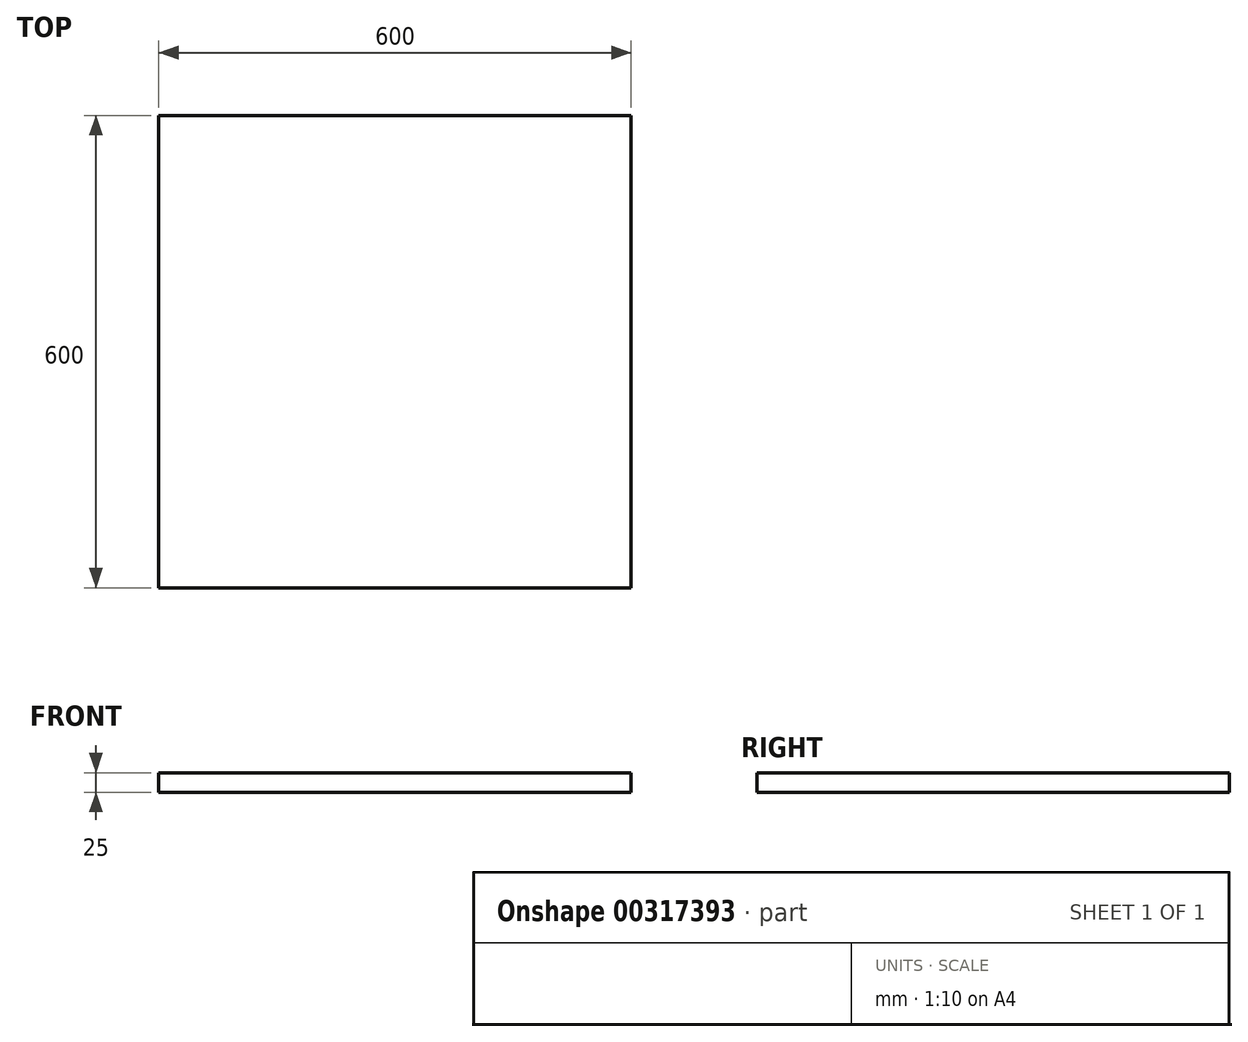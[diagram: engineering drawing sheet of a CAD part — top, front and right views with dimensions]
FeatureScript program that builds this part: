
annotation { "Feature Type Name" : "Feature", "Feature Type Description" : "" }
export const myFeature = defineFeature(function(context is Context, id is Id, definition is map)
    precondition{}
    {
        {
            var Q0;
            Q0=qCreatedBy(makeId("Top.planeOp"),FACE);
            var sketch = newSketch(context, id + "F0", { "sketchPlane" : qUnion([Q0])});
            skLineSegment(sketch, "E0.bottom", {"start": v(300, 300) * mm, "end": v(-300, 300) * mm});
            skLineSegment(sketch, "E0.top", {"start": v(300, -300) * mm, "end": v(-300, -300) * mm});
            skLineSegment(sketch, "E0.left", {"start": v(300, 300) * mm, "end": v(300, -300) * mm});
            skLineSegment(sketch, "E0.right", {"start": v(-300, 300) * mm, "end": v(-300, -300) * mm});
            skPoint(sketch, "E0.middle", {"position": v(0, 0) * mm});
            skSolve(sketch);
        }
        {
            var Q0;
            Q0 = qSketchRegion(id + "F0", true);
            extrude(context, id + "F1", {"entities" : qUnion([Q0]), "depth" : 25 * mm});
        }
    });
